# Revit family: Reece_Basin_Kado_Lussi_Wall Basin_1500 mm_Right Hand Bowl
name_source: partatom
category: Plumbing Fixtures
revit_build: Autodesk Revit 2018 (Build: 20170223_1515(x64)
units: mm (PartAtom-declared; Revit-internal decimal feet)

## family parameters
Cut with Voids When Loaded = Yes
Host = Face
Part Type = Normal
Room Calculation Point = Yes
Round Connector Dimension = Use Diameter
Shared = Yes

## types (1)
- No Taphole_Matte White
    Default Elevation = 0 mm  [stored 0 ft]
    Description = Kado Lussi 1500mm Single Wall Basin Right Hand Bowl with Overflow No Taphole Matte White Solid Surface
    Disclaimer = THIS FILE IS THE PROPERTY OF THE REECE GROUP. IT MAY NOT BE REPRODUCED, REVERSE-ENGINEERED OR MODIFIED. ANY REPUBLICATION, TRANSMISSION OR DISTRIBUTION FOR THE PURPOSE OF COMMERCIALLY EXPLOITING THE FILES IS PROHIBITED.
    Keynote = Product #1810640, Reece_Basin_Kado_Lussi_Wall Basin_1500 mm_Right Hand Bowl - No Taphole_Matte White
    Manufacturer = Kado
    Model = Lussi
    Reece_Basin_Outlet = 40 mm  [stored 0.131234 ft]
    Reece_Detail_Additional = Overflow
    Reece_Detail_Connector = No Taphole
    Reece_Detail_Disclaimer = THIS FILE IS THE PROPERTY OF THE REECE GROUP. IT MAY NOT BE REPRODUCED, REVERSE-ENGINEERED OR MODIFIED. ANY REPUBLICATION, TRANSMISSION OR DISTRIBUTION FOR THE PURPOSE OF COMMERCIALLY EXPLOITING THE FILES IS PROHIBITED.
    Reece_Detail_Installation = Wall Mounted
    Reece_Material_Main = Reece_Solid_Surface_Matte_White
    Reece_Overall_Capacity = 4.6 L
    Reece_Overall_Depth = 480 mm  [stored 1.5748 ft]
    Reece_Overall_Height = 126 mm
    Reece_Overall_Width = 1500 mm
    Reece_Product_Brand = Kado
    Reece_Product_Description = Kado Lussi 1500mm Single Right Hand Wall Basin Side Shelf with Overflow No Taphole Matte White Solid Surface
    Reece_Product_Mount = Wall Mounted
    Reece_Product_Number = 1810640
    Reece_Product_Sub Brand = Lussi
    Reece_Product_Type = Basin
    Reece_Product_Web Page = https://www.reece.com.au
    Reece_Taphole 0 = Yes
    Reece_Taphole 1 = No
    Type Comments = Basin
    URL = https://www.reece.com.au

note: [stored X ft] marks values corroborated as IEEE doubles in the binary element streams (Revit-internal decimal feet)

## geometry (parser evidence)
native form markers: Sweep x5
no freeform markers — native parametric forms only
